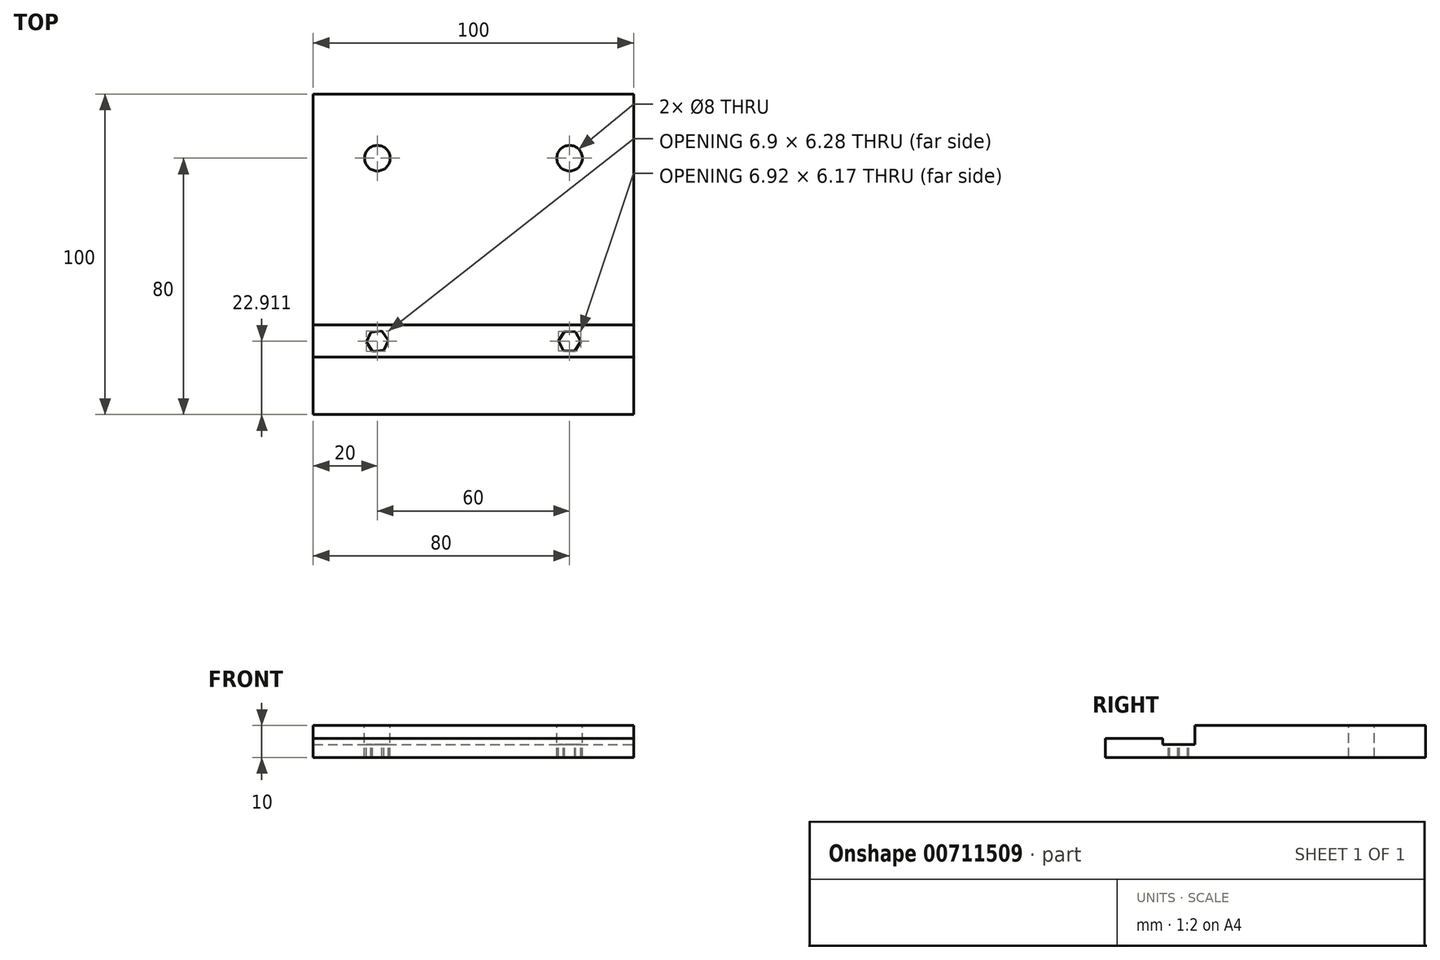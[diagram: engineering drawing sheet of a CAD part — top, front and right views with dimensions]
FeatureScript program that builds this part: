
annotation { "Feature Type Name" : "Feature", "Feature Type Description" : "" }
export const myFeature = defineFeature(function(context is Context, id is Id, definition is map)
    precondition{}
    {
        {
            var Q0;
            Q0=qCreatedBy(makeId("Top.planeOp"),FACE);
            var sketch = newSketch(context, id + "F0", { "sketchPlane" : qUnion([Q0])});
            skLineSegment(sketch, "E0.bottom", {"start": v(50, -50) * mm, "end": v(-50, -50) * mm});
            skLineSegment(sketch, "E0.top", {"start": v(50, 50) * mm, "end": v(-50, 50) * mm});
            skLineSegment(sketch, "E0.left", {"start": v(50, -50) * mm, "end": v(50, 50) * mm});
            skLineSegment(sketch, "E0.right", {"start": v(-50, -50) * mm, "end": v(-50, 50) * mm});
            skPoint(sketch, "E0.middle", {"position": v(0, 0) * mm});
            skSolve(sketch);
        }
        {
            var Q0;
            Q0 = qSketchRegion(id + "F0", true);
            extrude(context, id + "F1", {"entities" : qUnion([Q0]), "depth" : 4 * mm, "offsetDistance" : 25 * mm});
        }
        {
            var Q0;
            Q0=makeQuery(id+"F1.opExtrude","CAP_FACE",FACE,{"disambiguationData":[OSD([sQuery(id+"F0.wireOp",EDGE,"E0.bottom"),sQuery(id+"F0.wireOp",EDGE,"E0.top"),sQuery(id+"F0.wireOp",EDGE,"E0.left"),sQuery(id+"F0.wireOp",EDGE,"E0.right")])],"isStart":false});
            var sketch = newSketch(context, id + "F2", { "sketchPlane" : qUnion([Q0])});
            skLineSegment(sketch, "E1.bottom", {"start": v(-50, 50) * mm, "end": v(50, 50) * mm});
            skLineSegment(sketch, "E1.top", {"start": v(-50, -22) * mm, "end": v(50, -22) * mm});
            skLineSegment(sketch, "E1.left", {"start": v(-50, 50) * mm, "end": v(-50, -22) * mm});
            skLineSegment(sketch, "E1.right", {"start": v(50, 50) * mm, "end": v(50, -22) * mm});
            skLineSegment(sketch, "E2.bottom", {"start": v(-50, -50) * mm, "end": v(50, -50) * mm});
            skLineSegment(sketch, "E2.top", {"start": v(-50, -32) * mm, "end": v(50, -32) * mm});
            skLineSegment(sketch, "E2.left", {"start": v(-50, -50) * mm, "end": v(-50, -32) * mm});
            skLineSegment(sketch, "E2.right", {"start": v(50, -50) * mm, "end": v(50, -32) * mm});
            skSolve(sketch);
        }
        {
            var Q0;
            Q0 = qSketchRegion(id + "F2", true);
            extrude(context, id + "F3", {"entities" : qUnion([Q0]), "operationType" : NewBodyOperationType.ADD, "depth" : 2 * mm, "offsetDistance" : 25 * mm});
        }
        {
            var Q0;
            Q0=makeQuery(id+"F3.opExtrude","CAP_FACE",FACE,{"disambiguationData":[OSD([sQuery(id+"F2.wireOp",EDGE,"E1.bottom"),sQuery(id+"F2.wireOp",EDGE,"E1.top"),sQuery(id+"F2.wireOp",EDGE,"E1.left"),sQuery(id+"F2.wireOp",EDGE,"E1.right")])],"isStart":false});
            var sketch = newSketch(context, id + "F4", { "sketchPlane" : qUnion([Q0])});
            skLineSegment(sketch, "E3.bottom", {"start": v(-50, 50) * mm, "end": v(50, 50) * mm});
            skLineSegment(sketch, "E3.top", {"start": v(-50, -22) * mm, "end": v(50, -22) * mm});
            skLineSegment(sketch, "E3.left", {"start": v(-50, 50) * mm, "end": v(-50, -22) * mm});
            skLineSegment(sketch, "E3.right", {"start": v(50, 50) * mm, "end": v(50, -22) * mm});
            skSolve(sketch);
        }
        {
            var Q0;
            Q0 = qSketchRegion(id + "F4", true);
            extrude(context, id + "F5", {"entities" : qUnion([Q0]), "operationType" : NewBodyOperationType.ADD, "depth" : 4 * mm, "offsetDistance" : 25 * mm});
        }
        {
            var Q0;
            Q0=makeQuery(id+"F5.opExtrude","CAP_FACE",FACE,{"disambiguationData":[OSD([sQuery(id+"F4.wireOp",EDGE,"E3.bottom"),sQuery(id+"F4.wireOp",EDGE,"E3.top"),sQuery(id+"F4.wireOp",EDGE,"E3.left"),sQuery(id+"F4.wireOp",EDGE,"E3.right")])],"isStart":false});
            var sketch = newSketch(context, id + "F6", { "sketchPlane" : qUnion([Q0])});
            skCircle(sketch, "E4", {"center": v(30, 30) * mm, "radius": 4 * mm});
            skCircle(sketch, "E5", {"center": v(-30, 30) * mm, "radius": 4 * mm});
            skLineSegment(sketch, "E6", {"start": v(0, -22) * mm, "end": v(0, -32.18) * mm, "construction": true});
            skCircle(sketch, "E7.cCircle", {"center": v(-30, -27.09) * mm, "radius": 3 * mm});
            skLineSegment(sketch, "E7.0", {"start": v(-26.55, -26.78) * mm, "end": v(-28, -29.92) * mm});
            skLineSegment(sketch, "E7.1", {"start": v(-28, -29.92) * mm, "end": v(-31.46, -30.23) * mm});
            skLineSegment(sketch, "E7.2", {"start": v(-31.46, -30.23) * mm, "end": v(-33.45, -27.4) * mm});
            skLineSegment(sketch, "E7.3", {"start": v(-33.45, -27.4) * mm, "end": v(-32, -24.25) * mm});
            skLineSegment(sketch, "E7.4", {"start": v(-32, -24.25) * mm, "end": v(-28.54, -23.95) * mm});
            skLineSegment(sketch, "E7.5", {"start": v(-28.54, -23.95) * mm, "end": v(-26.55, -26.78) * mm});
            skPoint(sketch, "E7.0.midPoint", {"position": v(-27.28, -28.35) * mm});
            skPoint(sketch, "E8", {"position": v(0, -27.09) * mm});
            skLineSegment(sketch, "E9", {"start": v(-30, -27.09) * mm, "end": v(0, -27.09) * mm, "construction": true});
            skCircle(sketch, "E10.cCircle", {"center": v(30, -27.09) * mm, "radius": 3 * mm});
            skLineSegment(sketch, "E10.0", {"start": v(33.46, -27.27) * mm, "end": v(31.57, -30.18) * mm});
            skLineSegment(sketch, "E10.1", {"start": v(31.57, -30.18) * mm, "end": v(28.11, -30) * mm});
            skLineSegment(sketch, "E10.2", {"start": v(28.11, -30) * mm, "end": v(26.54, -26.9) * mm});
            skLineSegment(sketch, "E10.3", {"start": v(26.54, -26.9) * mm, "end": v(28.43, -24) * mm});
            skLineSegment(sketch, "E10.4", {"start": v(28.43, -24) * mm, "end": v(31.89, -24.18) * mm});
            skLineSegment(sketch, "E10.5", {"start": v(31.89, -24.18) * mm, "end": v(33.46, -27.27) * mm});
            skPoint(sketch, "E10.0.midPoint", {"position": v(32.52, -28.72) * mm});
            skSolve(sketch);
        }
        {
            var Q0;
            Q0 = qSketchRegion(id + "F6", true);
            extrude(context, id + "F7", {"entities" : qUnion([Q0]), "operationType" : NewBodyOperationType.REMOVE, "oppositeDirection" : true, "depth" : 25 * mm, "offsetDistance" : 25 * mm});
        }
    });
